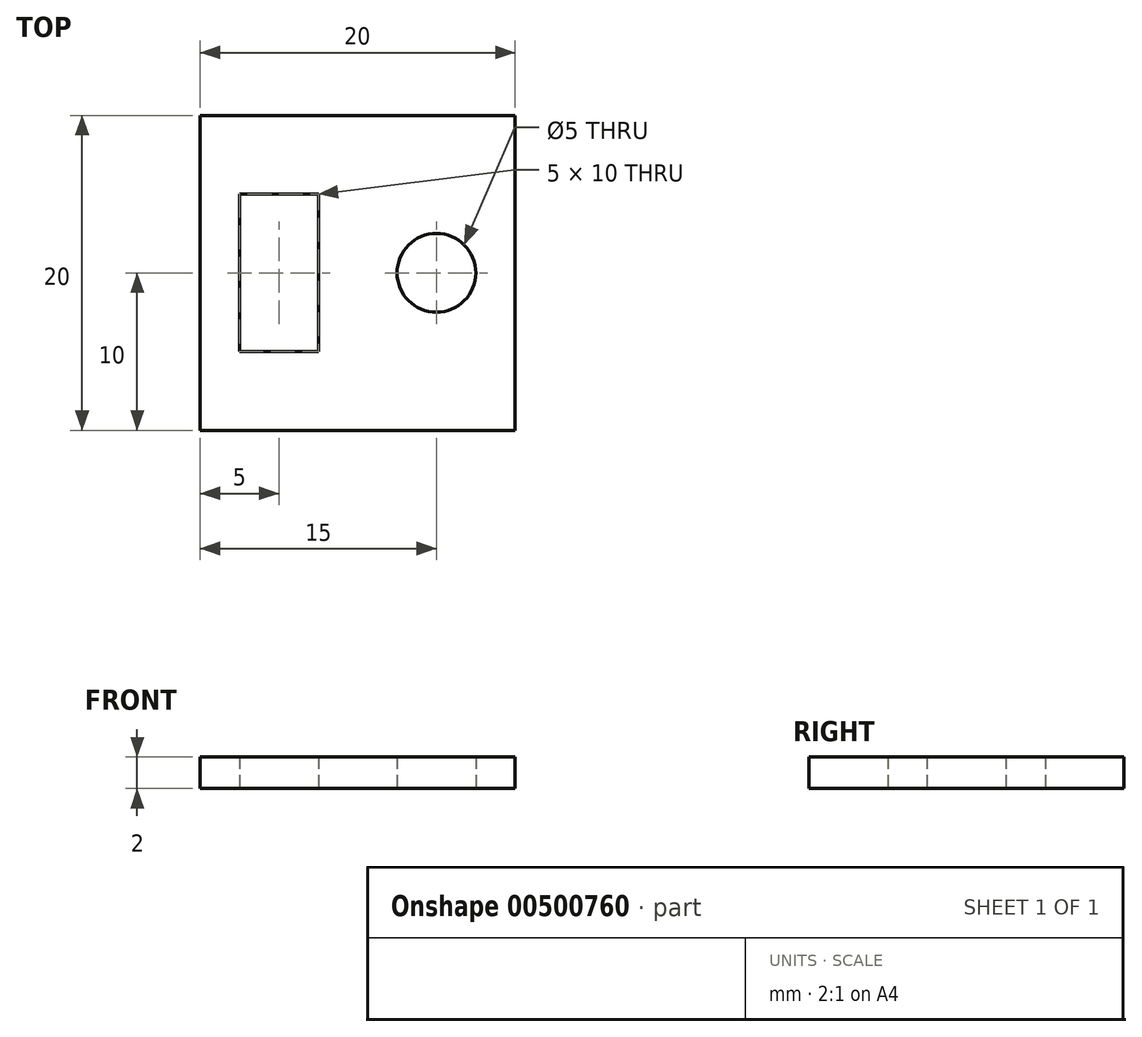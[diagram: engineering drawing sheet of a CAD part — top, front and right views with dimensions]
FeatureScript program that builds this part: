
annotation { "Feature Type Name" : "Feature", "Feature Type Description" : "" }
export const myFeature = defineFeature(function(context is Context, id is Id, definition is map)
    precondition{}
    {
        {
            var Q0;
            Q0=qCreatedBy(makeId("Top.planeOp"),FACE);
            var sketch = newSketch(context, id + "F0", { "sketchPlane" : qUnion([Q0])});
            skLineSegment(sketch, "E0.bottom", {"start": v(-10, 10) * mm, "end": v(10, 10) * mm});
            skLineSegment(sketch, "E0.top", {"start": v(-10, -10) * mm, "end": v(10, -10) * mm});
            skLineSegment(sketch, "E0.left", {"start": v(-10, 10) * mm, "end": v(-10, -10) * mm});
            skLineSegment(sketch, "E0.right", {"start": v(10, 10) * mm, "end": v(10, -10) * mm});
            skLineSegment(sketch, "E1.bottom", {"start": v(-7.5, 5) * mm, "end": v(-2.5, 5) * mm});
            skLineSegment(sketch, "E1.top", {"start": v(-7.5, -5) * mm, "end": v(-2.5, -5) * mm});
            skLineSegment(sketch, "E1.left", {"start": v(-7.5, 5) * mm, "end": v(-7.5, -5) * mm});
            skLineSegment(sketch, "E1.right", {"start": v(-2.5, 5) * mm, "end": v(-2.5, -5) * mm});
            skCircle(sketch, "E2", {"center": v(5, 0) * mm, "radius": 2.5 * mm});
            skSolve(sketch);
        }
        {
            var Q0;
            Q0=makeQuery(id+"F0.imprint","IMPRINT",FACE,{"disambiguationData":[TD([[makeQuery(id+"F0.imprint","IMPRINT",EDGE,{"derivedFrom":sQuery(id+"F0.wireOp",EDGE,"E0.bottom")}),-1.0]])]});
            extrude(context, id + "F1", {"entities" : qUnion([Q0]), "depth" : 2 * mm});
        }
    });
